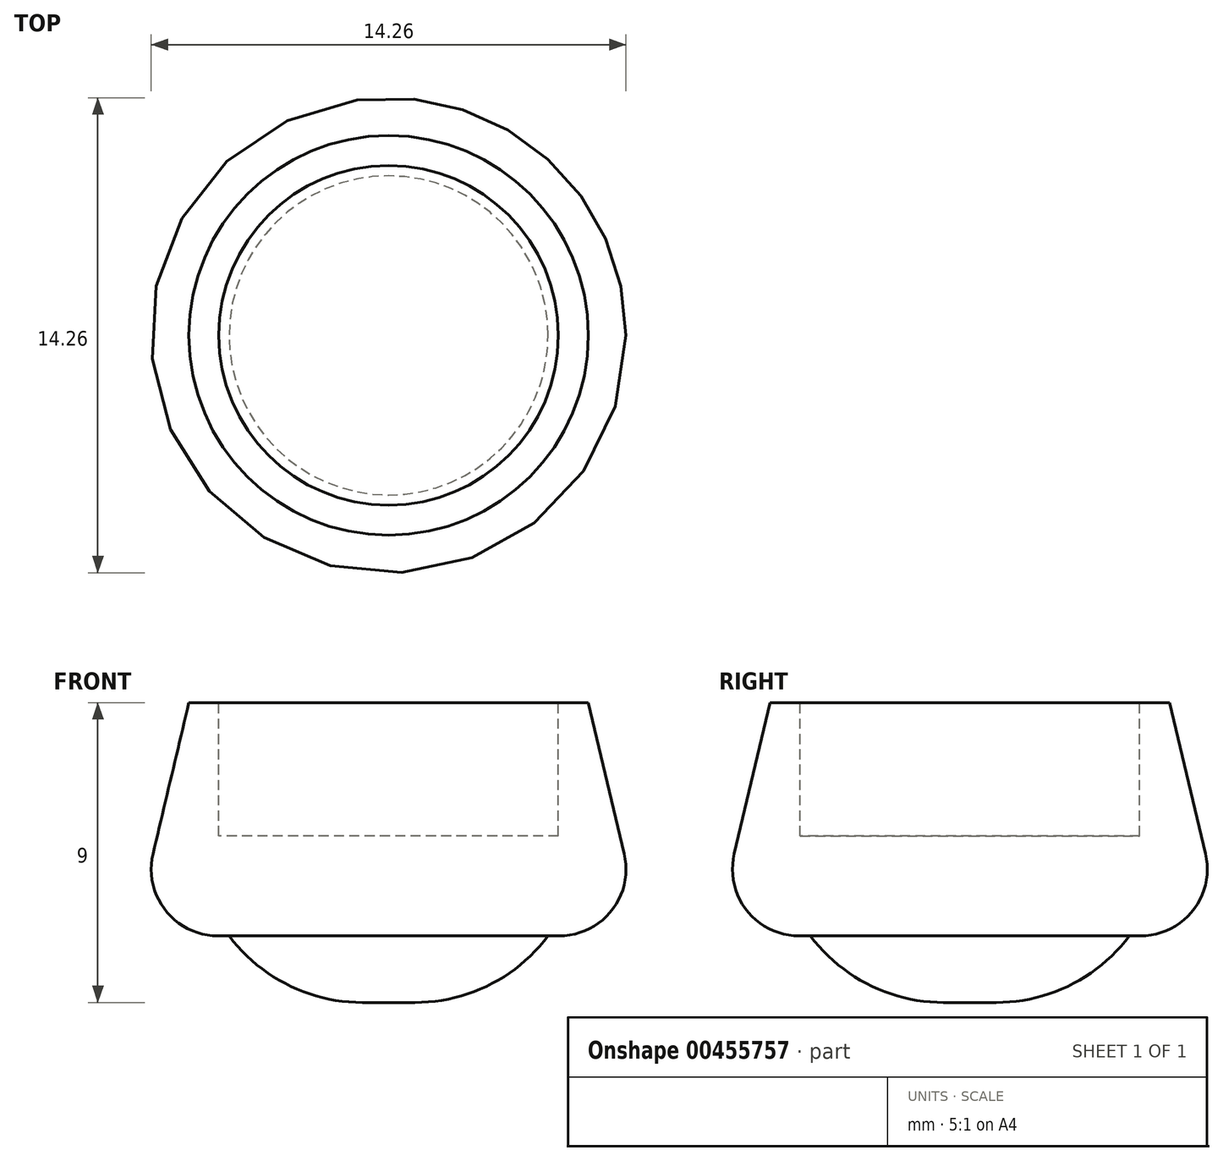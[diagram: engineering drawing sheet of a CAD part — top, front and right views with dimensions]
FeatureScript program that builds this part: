
annotation { "Feature Type Name" : "Feature", "Feature Type Description" : "" }
export const myFeature = defineFeature(function(context is Context, id is Id, definition is map)
    precondition{}
    {
        {
            var Q0;
            Q0=qCreatedBy(makeId("Top.planeOp"),FACE);
            var sketch = newSketch(context, id + "F0", { "sketchPlane" : qUnion([Q0])});
            skCircle(sketch, "E0", {"center": v(0, 0) * mm, "radius": 7.66 * mm});
            skSolve(sketch);
        }
        {
            var Q0;
            Q0=qCreatedBy(makeId("Top.planeOp"),FACE);
            cPlane(context, id + "F1", {"entities" : qUnion([Q0]), "cplaneType" : CPlaneType.OFFSET, "offset" : 7 * mm, "width" : 150 * mm, "height" : 150 * mm});
        }
        {
            var Q0;
            Q0=qCreatedBy(id+"F1.planeOp",FACE);
            var sketch = newSketch(context, id + "F2", { "sketchPlane" : qUnion([Q0])});
            skCircle(sketch, "E1", {"center": v(0, 0) * mm, "radius": 6 * mm});
            skSolve(sketch);
        }
        {
            var Q0;
            Q0=makeQuery(id+"F0.imprint","IMPRINT",FACE,{"disambiguationData":[TD([[makeQuery(id+"F0.imprint","IMPRINT",EDGE,{"derivedFrom":sQuery(id+"F0.wireOp",EDGE,"E0")}),1.0]])]});
            var Q1;
            Q1=makeQuery(id+"F2.imprint","IMPRINT",FACE,{"disambiguationData":[TD([[makeQuery(id+"F2.imprint","IMPRINT",EDGE,{"derivedFrom":sQuery(id+"F2.wireOp",EDGE,"E1")}),1.0]])]});
            loft(context, id + "F3", {"sheetProfilesArray" : [{ "sheetProfileEntities" : qUnion([Q0]) }, { "sheetProfileEntities" : qUnion([Q1]) }]});
        }
        {
            var Q0;
            Q0=makeQuery(id+"F3.opLoft","MID_CAP_EDGE",EDGE,{"disambiguationData":[OSD([sQuery(id+"F0.wireOp",EDGE,"E0")])],"capPos":0.0});
            fillet(context, id + "F4", {"entities" : qUnion([Q0]), "radius" : 2 * mm, "tangentPropagation" : true, "allowEdgeOverflow" : false});
        }
        {
            var Q0;
            Q0=makeQuery(id+"F3.opLoft","CAP_FACE",FACE,{"disambiguationData":[OSD([makeQuery(id+"F0.imprint","IMPRINT",FACE,{"disambiguationData":[TD([[makeQuery(id+"F0.imprint","IMPRINT",EDGE,{"derivedFrom":sQuery(id+"F0.wireOp",EDGE,"E0")}),1.0]])]})])],"isStart":true});
            var sketch = newSketch(context, id + "F5", { "sketchPlane" : qUnion([Q0])});
            skCircle(sketch, "E2", {"center": v(0, 0) * mm, "radius": 4.79 * mm});
            skSolve(sketch);
        }
        {
            var Q0;
            Q0 = qSketchRegion(id + "F5", true);
            extrude(context, id + "F6", {"entities" : qUnion([Q0]), "operationType" : NewBodyOperationType.ADD, "depth" : 2 * mm});
        }
        {
            var Q0;
            Q0=makeQuery(id+"F6.opExtrude","CAP_EDGE",EDGE,{"disambiguationData":[OSD([sQuery(id+"F5.wireOp",EDGE,"E2")])],"isStart":false});
            fillet(context, id + "F7", {"entities" : qUnion([Q0]), "radius" : 5 * mm, "tangentPropagation" : true, "allowEdgeOverflow" : false});
        }
        {
            var Q0;
            Q0=makeQuery(id+"F3.opLoft","CAP_FACE",FACE,{"disambiguationData":[OSD([makeQuery(id+"F2.imprint","IMPRINT",FACE,{"disambiguationData":[TD([[makeQuery(id+"F2.imprint","IMPRINT",EDGE,{"derivedFrom":sQuery(id+"F2.wireOp",EDGE,"E1")}),1.0]])]})])],"isStart":true});
            var sketch = newSketch(context, id + "F8", { "sketchPlane" : qUnion([Q0])});
            skCircle(sketch, "E3", {"center": v(0, 0) * mm, "radius": 5.1 * mm});
            skSolve(sketch);
        }
        {
            var Q0;
            Q0 = qSketchRegion(id + "F8", true);
            extrude(context, id + "F9", {"entities" : qUnion([Q0]), "operationType" : NewBodyOperationType.REMOVE, "oppositeDirection" : true, "depth" : 4 * mm});
        }
    });
